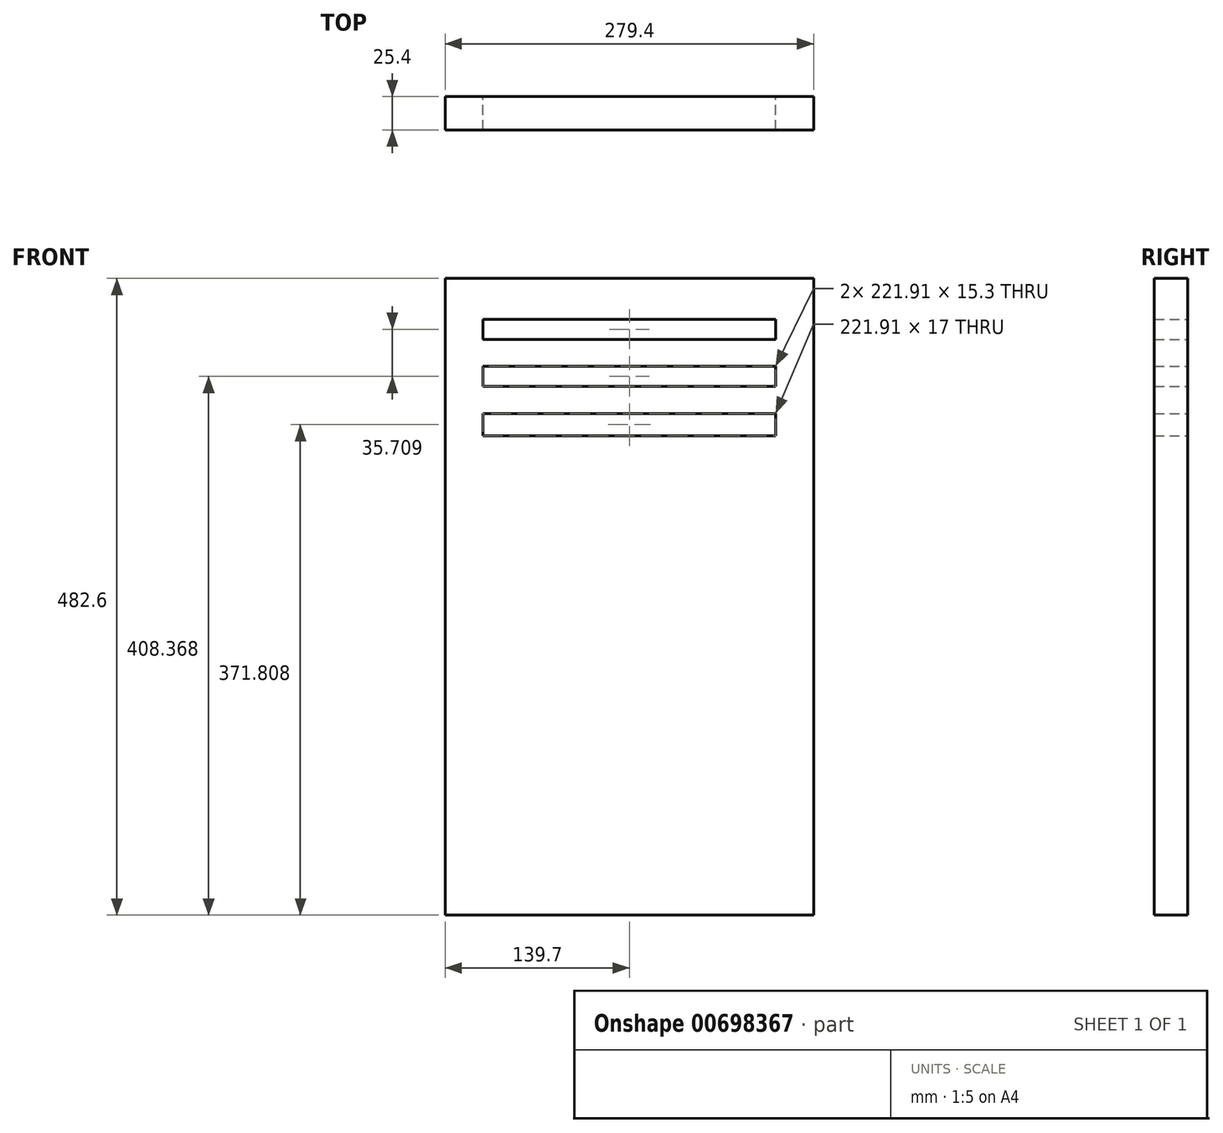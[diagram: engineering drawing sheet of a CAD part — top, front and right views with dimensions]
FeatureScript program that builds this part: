
annotation { "Feature Type Name" : "Feature", "Feature Type Description" : "" }
export const myFeature = defineFeature(function(context is Context, id is Id, definition is map)
    precondition{}
    {
        {
            var Q0;
            Q0=qCreatedBy(makeId("Front.planeOp"),FACE);
            var sketch = newSketch(context, id + "F0", { "sketchPlane" : qUnion([Q0])});
            skLineSegment(sketch, "E0.bottom", {"start": v(-139.7, 241.3) * mm, "end": v(139.7, 241.3) * mm});
            skLineSegment(sketch, "E0.top", {"start": v(-139.7, -241.3) * mm, "end": v(139.7, -241.3) * mm});
            skLineSegment(sketch, "E0.left", {"start": v(-139.7, 241.3) * mm, "end": v(-139.7, -241.3) * mm});
            skLineSegment(sketch, "E0.right", {"start": v(139.7, 241.3) * mm, "end": v(139.7, -241.3) * mm});
            skPoint(sketch, "E0.middle", {"position": v(0, 0) * mm});
            skSolve(sketch);
        }
        {
            var Q0;
            Q0=makeQuery(id+"F0.imprint","IMPRINT",FACE,{"disambiguationData":[TD([[makeQuery(id+"F0.imprint","IMPRINT",EDGE,{"derivedFrom":sQuery(id+"F0.wireOp",EDGE,"E0.bottom")}),-1.0]])]});
            var sketch = newSketch(context, id + "F1", { "sketchPlane" : qUnion([Q0])});
            skLineSegment(sketch, "E1.bottom", {"start": v(-110.95, 210.43) * mm, "end": v(110.95, 210.43) * mm});
            skLineSegment(sketch, "E1.top", {"start": v(-110.95, 195.13) * mm, "end": v(110.95, 195.13) * mm});
            skLineSegment(sketch, "E1.left", {"start": v(-110.95, 210.43) * mm, "end": v(-110.95, 195.13) * mm});
            skLineSegment(sketch, "E1.right", {"start": v(110.95, 210.43) * mm, "end": v(110.95, 195.13) * mm});
            skPoint(sketch, "E1.middle", {"position": v(0, 202.78) * mm});
            skLineSegment(sketch, "E2.bottom", {"start": v(-110.95, 174.72) * mm, "end": v(110.95, 174.72) * mm});
            skLineSegment(sketch, "E2.top", {"start": v(-110.95, 159.42) * mm, "end": v(110.95, 159.42) * mm});
            skLineSegment(sketch, "E2.left", {"start": v(-110.95, 174.72) * mm, "end": v(-110.95, 159.42) * mm});
            skLineSegment(sketch, "E2.right", {"start": v(110.95, 174.72) * mm, "end": v(110.95, 159.42) * mm});
            skPoint(sketch, "E2.middle", {"position": v(0, 167.07) * mm});
            skLineSegment(sketch, "E3.bottom", {"start": v(-110.95, 139.01) * mm, "end": v(110.95, 139.01) * mm});
            skLineSegment(sketch, "E3.top", {"start": v(-110.95, 122) * mm, "end": v(110.95, 122) * mm});
            skLineSegment(sketch, "E3.left", {"start": v(-110.95, 139.01) * mm, "end": v(-110.95, 122) * mm});
            skLineSegment(sketch, "E3.right", {"start": v(110.95, 139.01) * mm, "end": v(110.95, 122) * mm});
            skPoint(sketch, "E3.middle", {"position": v(0, 130.5) * mm});
            skSolve(sketch);
        }
        {
            var Q0;
            Q0=makeQuery(id+"F1.imprint","IMPRINT",FACE,{"disambiguationData":[TD([[makeQuery(id+"F1.imprint","IMPRINT",EDGE,{"derivedFrom":sQuery(id+"F1.wireOp",EDGE,"E1.bottom")}),1.0]])]});
            extrude(context, id + "F2", {"entities" : qUnion([Q0]), "depth" : 25.4 * mm, "offsetDistance" : 25.4 * mm});
        }
    });
